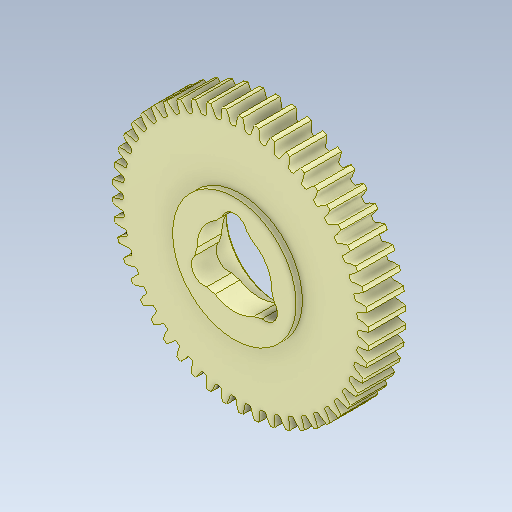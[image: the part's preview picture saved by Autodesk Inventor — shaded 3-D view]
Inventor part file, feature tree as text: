
AUTODESK INVENTOR PART (.ipt)
format: ipt  version: 2020 (Build 240168000, 168)  size: 542,208 bytes
history: native  units: in
note: dims shown in document units (in); Inventor stores cm internally (conversion verified against a paired STEP export)
features: chamfer x1
ambient origin geometry x8: Origin, YZ Plane, XZ Plane, XY Plane, X Axis, Y Axis, Z Axis, Center Point
bodies: Solid1 (feature_tree)
feature tree (1):
  chamfer  "Chamfer1"  [1 undecoded]
note: 1 required parameter value undecoded (feature->parameter linkage not recoverable at this tier; creation-order binding heuristic only, values carry confidence <= 0.55)
